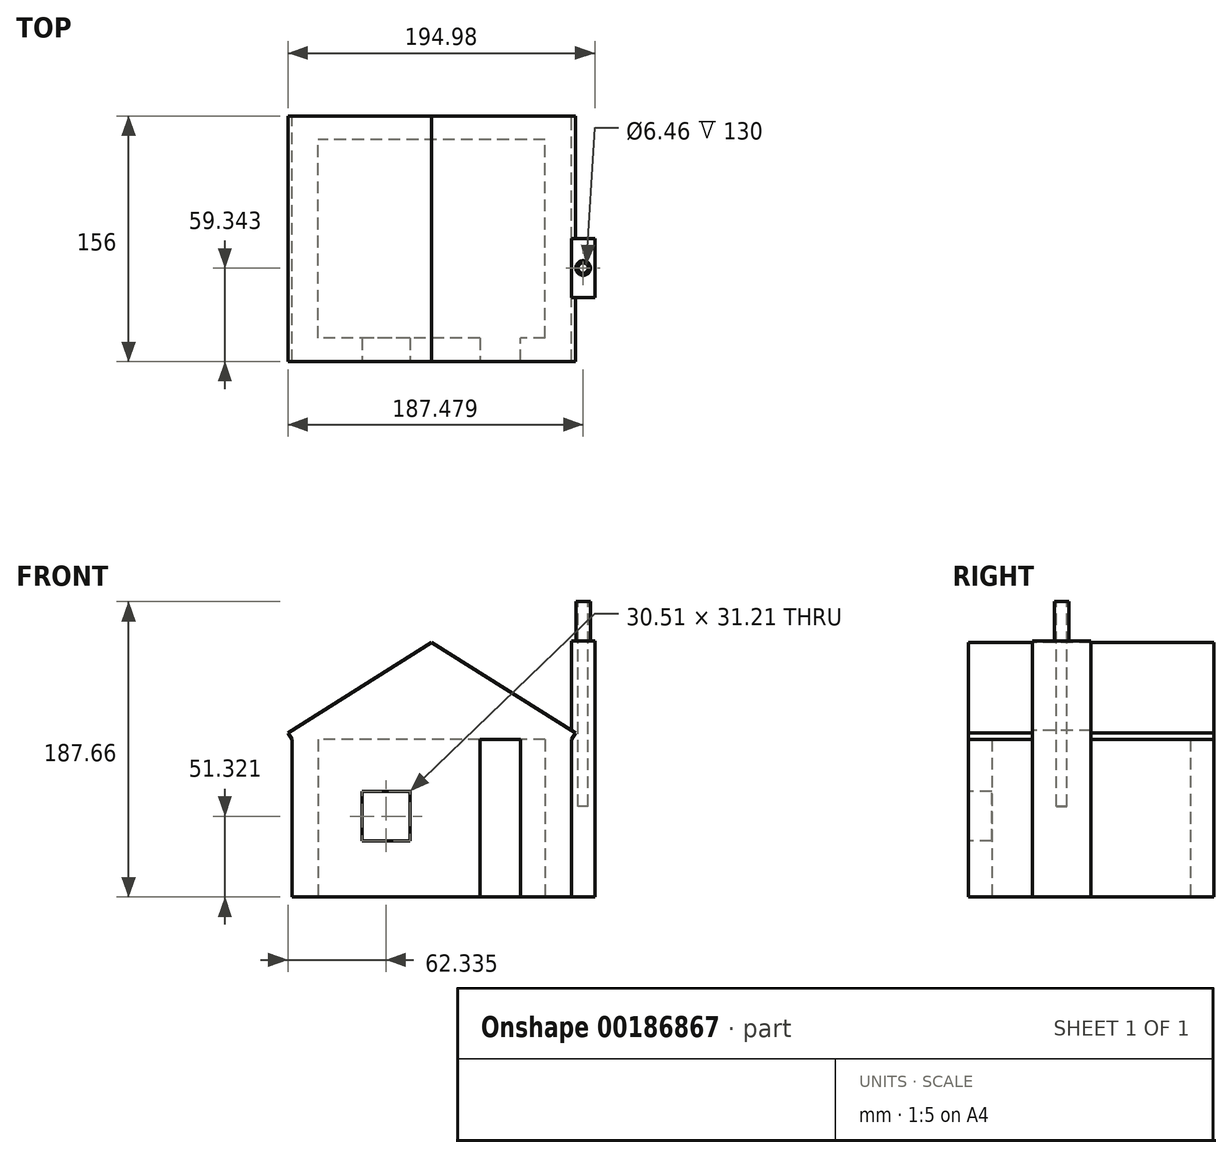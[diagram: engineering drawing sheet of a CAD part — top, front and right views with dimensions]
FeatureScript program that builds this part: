
annotation { "Feature Type Name" : "Feature", "Feature Type Description" : "" }
export const myFeature = defineFeature(function(context is Context, id is Id, definition is map)
    precondition{}
    {
        {
            var Q0;
            Q0=qCreatedBy(makeId("Top.planeOp"),FACE);
            var sketch = newSketch(context, id + "F0", { "sketchPlane" : qUnion([Q0])});
            skLineSegment(sketch, "E0.bottom", {"start": v(88.66, -78) * mm, "end": v(-88.66, -78) * mm});
            skLineSegment(sketch, "E0.top", {"start": v(88.66, 78) * mm, "end": v(-88.66, 78) * mm});
            skLineSegment(sketch, "E0.left", {"start": v(88.66, -78) * mm, "end": v(88.66, 78) * mm});
            skLineSegment(sketch, "E0.right", {"start": v(-88.66, -78) * mm, "end": v(-88.66, 78) * mm});
            skPoint(sketch, "E0.middle", {"position": v(0, 0) * mm});
            skLineSegment(sketch, "E1.bottom", {"start": v(72.04, -63.08) * mm, "end": v(-72.04, -63.08) * mm});
            skLineSegment(sketch, "E1.top", {"start": v(72.04, 63.08) * mm, "end": v(-72.04, 63.08) * mm});
            skLineSegment(sketch, "E1.left", {"start": v(72.04, -63.08) * mm, "end": v(72.04, 63.08) * mm});
            skLineSegment(sketch, "E1.right", {"start": v(-72.04, -63.08) * mm, "end": v(-72.04, 63.08) * mm});
            skLineSegment(sketch, "E2", {"start": v(30.69, -63.08) * mm, "end": v(30.69, -78) * mm});
            skLineSegment(sketch, "E3", {"start": v(56.26, -78) * mm, "end": v(56.26, -63.08) * mm});
            skSolve(sketch);
        }
        {
            var Q0;
            Q0=makeQuery(id+"F0.imprint","IMPRINT",FACE,{"disambiguationData":[TD([[makeQuery(id+"F0.imprint","IMPRINT",EDGE,{"derivedFrom":sQuery(id+"F0.wireOp",EDGE,"E0.top")}),1.0]])]});
            extrude(context, id + "F1", {"entities" : qUnion([Q0]), "depth" : 100 * mm});
        }
        {
            var Q0;
            {var subQ0=sQuery(id+"F0.wireOp",EDGE,"E0.bottom");Q0=makeQuery(id+"F1.opExtrude","SWEPT_FACE",FACE,{"disambiguationData":[OSD([subQ0]),TDD([makeQuery(id+"F0.imprint","IMPRINT",EDGE,{"disambiguationData":[TD([[makeQuery(id+"F0.imprint","INTERSECT",VERTEX,{"derivedFrom":[subQ0,sQuery(id+"F0.wireOp",EDGE,"E0.right")]}),1.0]])],"derivedFrom":subQ0})])]});}
            var sketch = newSketch(context, id + "F2", { "sketchPlane" : qUnion([Q0])});
            skLineSegment(sketch, "E4.bottom", {"start": v(-13.73, 35.72) * mm, "end": v(-44.24, 35.72) * mm});
            skLineSegment(sketch, "E4.top", {"start": v(-13.73, 66.92) * mm, "end": v(-44.24, 66.92) * mm});
            skLineSegment(sketch, "E4.left", {"start": v(-13.73, 35.72) * mm, "end": v(-13.73, 66.92) * mm});
            skLineSegment(sketch, "E4.right", {"start": v(-44.24, 35.72) * mm, "end": v(-44.24, 66.92) * mm});
            skPoint(sketch, "E4.middle", {"position": v(-28.98, 51.32) * mm});
            skPoint(sketch, "E4.middle.positionSnap0", {"position": v(-28.98, 0) * mm});
            skPoint(sketch, "E4.centerSnap0", {"position": v(-28.98, 0) * mm});
            skSolve(sketch);
        }
        {
            var Q0;
            Q0 = qSketchRegion(id + "F2", true);
            extrude(context, id + "F3", {"entities" : qUnion([Q0]), "operationType" : NewBodyOperationType.REMOVE, "oppositeDirection" : true, "depth" : 25 * mm});
        }
        {
            var Q0;
            {var subQ0=sQuery(id+"F0.wireOp",EDGE,"E0.bottom");Q0=makeQuery(id+"F1.opExtrude","SWEPT_FACE",FACE,{"disambiguationData":[OSD([subQ0]),TDD([makeQuery(id+"F0.imprint","IMPRINT",EDGE,{"disambiguationData":[TD([[makeQuery(id+"F0.imprint","INTERSECT",VERTEX,{"derivedFrom":[subQ0,sQuery(id+"F0.wireOp",EDGE,"E0.right")]}),1.0]])],"derivedFrom":subQ0})])]});}
            var sketch = newSketch(context, id + "F4", { "sketchPlane" : qUnion([Q0])});
            skLineSegment(sketch, "E5", {"start": v(0, 155.68) * mm, "end": v(-88.66, 100) * mm});
            skLineSegment(sketch, "E6.0", {"start": v(30.69, 100) * mm, "end": v(-88.66, 100) * mm});
            skLineSegment(sketch, "E7.0", {"start": v(88.66, 100) * mm, "end": v(56.26, 100) * mm});
            skLineSegment(sketch, "E8", {"start": v(0, 155.68) * mm, "end": v(88.66, 100) * mm});
            skLineSegment(sketch, "E9", {"start": v(56.26, 100) * mm, "end": v(30.69, 100) * mm});
            skLineSegment(sketch, "E10.0", {"start": v(0, 161.58) * mm, "end": v(-91.32, 104.23) * mm});
            skLineSegment(sketch, "E10.1", {"start": v(0, 161.58) * mm, "end": v(91.32, 104.23) * mm});
            skLineSegment(sketch, "E11", {"start": v(-91.32, 104.23) * mm, "end": v(-88.66, 100) * mm});
            skLineSegment(sketch, "E12", {"start": v(88.66, 100) * mm, "end": v(91.32, 104.23) * mm});
            skSolve(sketch);
        }
        {
            var Q0;
            Q0=makeQuery(id+"F4.imprint","IMPRINT",FACE,{"disambiguationData":[TD([[makeQuery(id+"F4.imprint","IMPRINT",EDGE,{"derivedFrom":sQuery(id+"F4.wireOp",EDGE,"E5")}),1.0]])]});
            var Q1;
            Q1=makeQuery(id+"F1.opExtrude","SWEPT_FACE",FACE,{"disambiguationData":[OSD([sQuery(id+"F0.wireOp",EDGE,"E0.top")])]});
            extrude(context, id + "F5", {"entities" : qUnion([Q0]), "operationType" : NewBodyOperationType.ADD, "endBound" : BoundingType.UP_TO_SURFACE, "oppositeDirection" : true, "endBoundEntityFace" : qUnion([Q1]), "depth" : 25 * mm});
        }
        {
            var Q0;
            Q0=makeQuery(id+"F4.imprint","IMPRINT",FACE,{"disambiguationData":[TD([[makeQuery(id+"F4.imprint","IMPRINT",EDGE,{"derivedFrom":sQuery(id+"F4.wireOp",EDGE,"E5")}),-1.0]])]});
            var Q1;
            {var subQ0=sQuery(id+"F0.wireOp",EDGE,"E0.top");Q1=makeQuery(id+"F5.boolean.opBoolean","MERGE",FACE,{"derivedFrom":[makeQuery(id+"F1.opExtrude","SWEPT_FACE",FACE,{"disambiguationData":[OSD([subQ0])]}),makeQuery(id+"F5.opExtrude","CAP_FACE",FACE,{"disambiguationData":[OSD([subQ0])],"isStart":false})]});}
            extrude(context, id + "F6", {"entities" : qUnion([Q0]), "operationType" : NewBodyOperationType.ADD, "endBound" : BoundingType.UP_TO_SURFACE, "oppositeDirection" : true, "endBoundEntityFace" : qUnion([Q1]), "depth" : 25 * mm});
        }
        {
            var Q0;
            Q0=makeQuery(id+"F1.opExtrude","SWEPT_FACE",FACE,{"disambiguationData":[OSD([sQuery(id+"F0.wireOp",EDGE,"E0.left")])]});
            var sketch = newSketch(context, id + "F7", { "sketchPlane" : qUnion([Q0])});
            skLineSegment(sketch, "E13.bottom", {"start": v(0, 0) * mm, "end": v(-37.31, 0) * mm});
            skLineSegment(sketch, "E13.top", {"start": v(0, 162.66) * mm, "end": v(-37.31, 162.66) * mm});
            skLineSegment(sketch, "E13.left", {"start": v(0, 0) * mm, "end": v(0, 162.66) * mm});
            skLineSegment(sketch, "E13.right", {"start": v(-37.31, 0) * mm, "end": v(-37.31, 162.66) * mm});
            skSolve(sketch);
        }
        {
            var Q0;
            {var subQ0=sQuery(id+"F7.wireOp",EDGE,"E13.bottom");Q0=makeQuery(id+"F7.imprint","IMPRINT",FACE,{"disambiguationData":[TD([[makeQuery(id+"F7.imprint","IMPRINT",EDGE,{"derivedFrom":subQ0}),1.0]])]});}
            var Q1;
            {var subQ0=sQuery(id+"F7.wireOp",EDGE,"E13.top");Q1=makeQuery(id+"F7.imprint","IMPRINT",FACE,{"disambiguationData":[TD([[makeQuery(id+"F7.imprint","IMPRINT",EDGE,{"derivedFrom":subQ0}),1.0]])]});}
            extrude(context, id + "F8", {"entities" : qUnion([Q0, Q1]), "operationType" : NewBodyOperationType.ADD, "depth" : 15 * mm});
        }
        {
            var Q0;
            Q0=makeQuery(id+"F8.opExtrude","SWEPT_FACE",FACE,{"disambiguationData":[OSD([sQuery(id+"F7.wireOp",EDGE,"E13.top")])]});
            var sketch = newSketch(context, id + "F9", { "sketchPlane" : qUnion([Q0])});
            skCircle(sketch, "E14", {"center": v(96.16, -18.66) * mm, "radius": 4.66 * mm});
            skPoint(sketch, "E14.centerSnap0", {"position": v(96.16, -37.31) * mm});
            skPoint(sketch, "E14.centerSnap1", {"position": v(103.66, -18.66) * mm});
            skSolve(sketch);
        }
        {
            var Q0;
            Q0=makeQuery(id+"F9.imprint","IMPRINT",FACE,{"disambiguationData":[TD([[makeQuery(id+"F9.imprint","IMPRINT",EDGE,{"derivedFrom":sQuery(id+"F9.wireOp",EDGE,"E14")}),1.0]])]});
            extrude(context, id + "F10", {"entities" : qUnion([Q0]), "operationType" : NewBodyOperationType.ADD, "depth" : 25 * mm});
        }
        {
            var Q0;
            Q0=makeQuery(id+"F10.opExtrude","CAP_FACE",FACE,{"disambiguationData":[OSD([sQuery(id+"F9.wireOp",EDGE,"E14")])],"isStart":false});
            var sketch = newSketch(context, id + "F11", { "sketchPlane" : qUnion([Q0])});
            skCircle(sketch, "E15", {"center": v(96.16, -18.66) * mm, "radius": 3.23 * mm});
            skSolve(sketch);
        }
        {
            var Q0;
            Q0=makeQuery(id+"F11.imprint","IMPRINT",FACE,{"disambiguationData":[TD([[makeQuery(id+"F11.imprint","IMPRINT",EDGE,{"derivedFrom":sQuery(id+"F11.wireOp",EDGE,"E15")}),1.0]])]});
            extrude(context, id + "F12", {"entities" : qUnion([Q0]), "operationType" : NewBodyOperationType.REMOVE, "oppositeDirection" : true, "depth" : 130 * mm});
        }
    });
